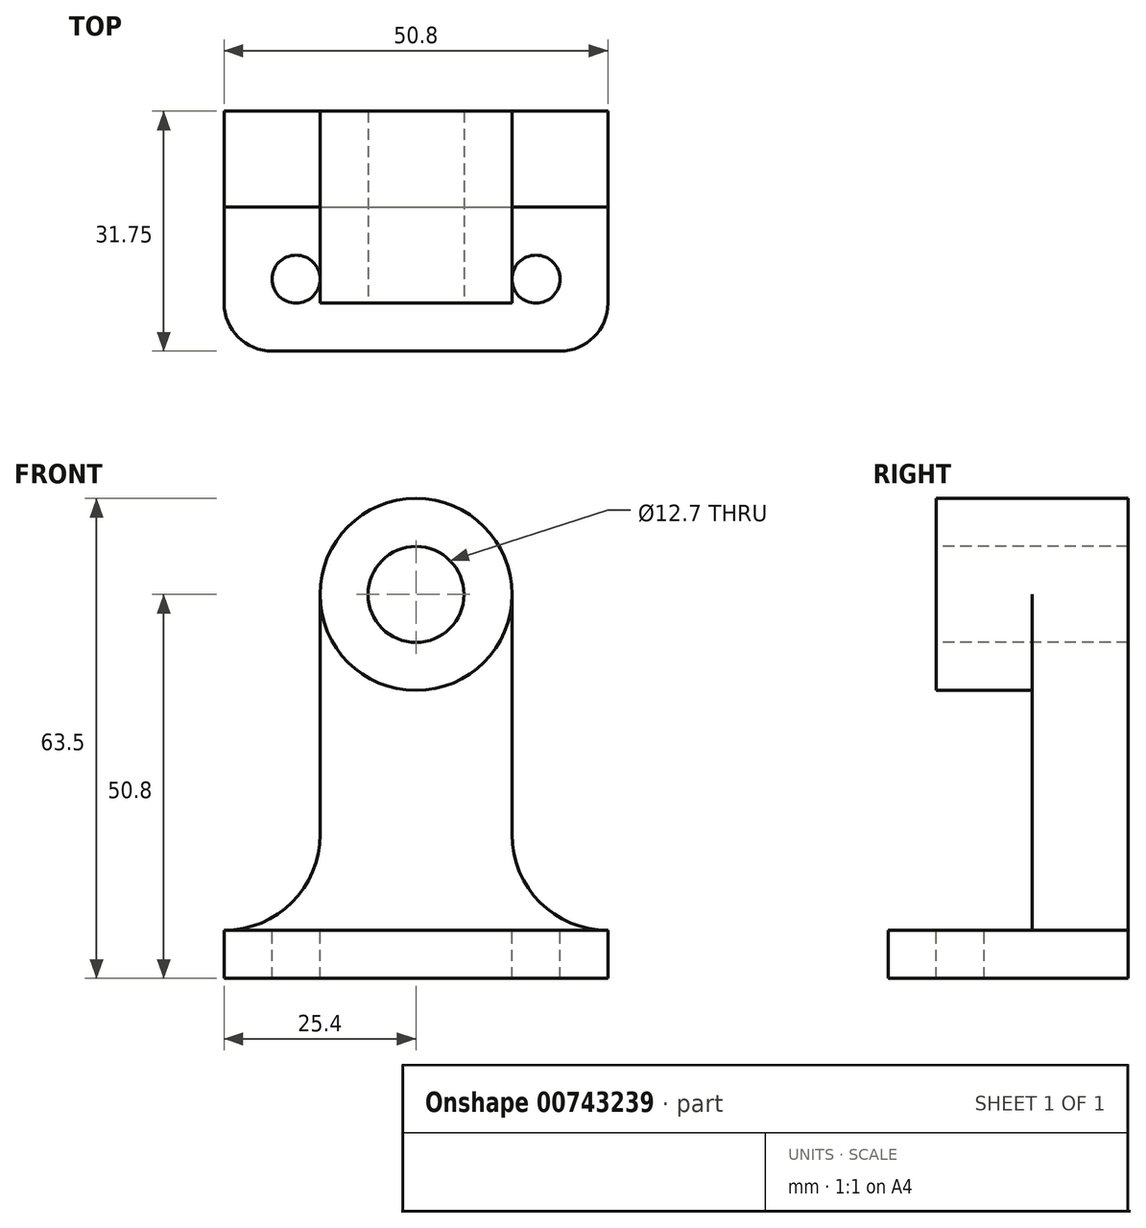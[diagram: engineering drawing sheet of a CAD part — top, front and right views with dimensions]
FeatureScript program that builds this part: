
annotation { "Feature Type Name" : "Feature", "Feature Type Description" : "" }
export const myFeature = defineFeature(function(context is Context, id is Id, definition is map)
    precondition{}
    {
        {
            var Q0;
            Q0=qCreatedBy(makeId("Top.planeOp"),FACE);
            var sketch = newSketch(context, id + "F0", { "sketchPlane" : qUnion([Q0])});
            skLineSegment(sketch, "E0.bottom", {"start": v(0, 0) * mm, "end": v(50.8, 0) * mm});
            skLineSegment(sketch, "E0.top", {"start": v(0, -25.4) * mm, "end": v(50.8, -25.4) * mm});
            skLineSegment(sketch, "E0.left", {"start": v(0, 0) * mm, "end": v(0, -25.4) * mm});
            skLineSegment(sketch, "E0.right", {"start": v(50.8, 0) * mm, "end": v(50.8, -25.4) * mm});
            skCircle(sketch, "E1", {"center": v(6.35, -25.4) * mm, "radius": 6.35 * mm});
            skCircle(sketch, "E2", {"center": v(44.45, -25.4) * mm, "radius": 6.35 * mm});
            skLineSegment(sketch, "E3.bottom", {"start": v(6.35, -25.4) * mm, "end": v(44.45, -25.4) * mm});
            skLineSegment(sketch, "E3.top", {"start": v(6.35, -31.75) * mm, "end": v(44.45, -31.75) * mm});
            skLineSegment(sketch, "E3.left", {"start": v(6.35, -25.4) * mm, "end": v(6.35, -31.75) * mm});
            skLineSegment(sketch, "E3.right", {"start": v(44.45, -25.4) * mm, "end": v(44.45, -31.75) * mm});
            skSolve(sketch);
        }
        {
            var Q0;
            Q0=makeQuery(id+"F0.imprint","IMPRINT",FACE,{"disambiguationData":[TD([[makeQuery(id+"F0.imprint","IMPRINT",EDGE,{"derivedFrom":sQuery(id+"F0.wireOp",EDGE,"E0.bottom")}),-1.0]])]});
            var Q1;
            {var subQ0=sQuery(id+"F0.wireOp",EDGE,"E1");var subQ3=sQuery(id+"F0.wireOp",EDGE,"E3.bottom");var subQ5=makeQuery(id+"F0.imprint","INTERSECT",VERTEX,{"derivedFrom":[subQ0,subQ3]});Q1=makeQuery(id+"F0.imprint","IMPRINT",FACE,{"disambiguationData":[TD([[makeQuery(id+"F0.imprint","IMPRINT",EDGE,{"disambiguationData":[TD([[subQ5,-1.0]])],"derivedFrom":subQ0}),1.0]])]});}
            var Q2;
            {var subQ3=sQuery(id+"F0.wireOp",EDGE,"E3.left");Q2=makeQuery(id+"F0.imprint","IMPRINT",FACE,{"disambiguationData":[TD([[makeQuery(id+"F0.imprint","IMPRINT",EDGE,{"derivedFrom":subQ3}),-1.0]])]});}
            var Q3;
            {var subQ0=sQuery(id+"F0.wireOp",EDGE,"E3.left");Q3=makeQuery(id+"F0.imprint","IMPRINT",FACE,{"disambiguationData":[TD([[makeQuery(id+"F0.imprint","IMPRINT",EDGE,{"derivedFrom":subQ0}),1.0]])]});}
            var Q4;
            {var subQ0=sQuery(id+"F0.wireOp",EDGE,"E3.top");Q4=makeQuery(id+"F0.imprint","IMPRINT",FACE,{"disambiguationData":[TD([[makeQuery(id+"F0.imprint","IMPRINT",EDGE,{"derivedFrom":subQ0}),1.0]])]});}
            var Q5;
            {var subQ0=sQuery(id+"F0.wireOp",EDGE,"E3.right");Q5=makeQuery(id+"F0.imprint","IMPRINT",FACE,{"disambiguationData":[TD([[makeQuery(id+"F0.imprint","IMPRINT",EDGE,{"derivedFrom":subQ0}),-1.0]])]});}
            var Q6;
            {var subQ3=sQuery(id+"F0.wireOp",EDGE,"E3.right");Q6=makeQuery(id+"F0.imprint","IMPRINT",FACE,{"disambiguationData":[TD([[makeQuery(id+"F0.imprint","IMPRINT",EDGE,{"derivedFrom":subQ3}),1.0]])]});}
            var Q7;
            {var subQ0=sQuery(id+"F0.wireOp",EDGE,"E2");var subQ3=sQuery(id+"F0.wireOp",EDGE,"E3.bottom");var subQ5=makeQuery(id+"F0.imprint","INTERSECT",VERTEX,{"derivedFrom":[subQ0,subQ3]});Q7=makeQuery(id+"F0.imprint","IMPRINT",FACE,{"disambiguationData":[TD([[makeQuery(id+"F0.imprint","IMPRINT",EDGE,{"disambiguationData":[TD([[subQ5,1.0]])],"derivedFrom":subQ0}),1.0]])]});}
            extrude(context, id + "F1", {"entities" : qUnion([Q0, Q1, Q2, Q3, Q4, Q5, Q6, Q7]), "depth" : 6.35 * mm, "offsetDistance" : 25.4 * mm});
        }
        {
            var Q0;
            Q0=qCreatedBy(makeId("Front.planeOp"),FACE);
            var sketch = newSketch(context, id + "F2", { "sketchPlane" : qUnion([Q0])});
            skLineSegment(sketch, "E4.bottom", {"start": v(12.7, 6.35) * mm, "end": v(38.1, 6.35) * mm});
            skLineSegment(sketch, "E4.top", {"start": v(12.7, 50.8) * mm, "end": v(38.1, 50.8) * mm});
            skLineSegment(sketch, "E4.left", {"start": v(12.7, 6.35) * mm, "end": v(12.7, 50.8) * mm});
            skLineSegment(sketch, "E4.right", {"start": v(38.1, 6.35) * mm, "end": v(38.1, 50.8) * mm});
            skCircle(sketch, "E5", {"center": v(25.4, 50.8) * mm, "radius": 12.7 * mm});
            skLineSegment(sketch, "E6.bottom", {"start": v(12.7, 50.8) * mm, "end": v(0, 50.8) * mm});
            skLineSegment(sketch, "E6.top", {"start": v(12.7, 6.35) * mm, "end": v(0, 6.35) * mm});
            skLineSegment(sketch, "E6.left", {"start": v(12.7, 50.8) * mm, "end": v(12.7, 6.35) * mm});
            skLineSegment(sketch, "E6.right", {"start": v(0, 50.8) * mm, "end": v(0, 6.35) * mm});
            skLineSegment(sketch, "E7.bottom", {"start": v(38.1, 50.8) * mm, "end": v(50.8, 50.8) * mm});
            skLineSegment(sketch, "E7.top", {"start": v(38.1, 6.35) * mm, "end": v(50.8, 6.35) * mm});
            skLineSegment(sketch, "E7.left", {"start": v(38.1, 50.8) * mm, "end": v(38.1, 6.35) * mm});
            skLineSegment(sketch, "E7.right", {"start": v(50.8, 50.8) * mm, "end": v(50.8, 6.35) * mm});
            skCircle(sketch, "E8", {"center": v(50.8, 19.05) * mm, "radius": 12.7 * mm});
            skCircle(sketch, "E9", {"center": v(0, 19.05) * mm, "radius": 12.7 * mm});
            skSolve(sketch);
        }
        {
            var Q0;
            {var subQ1=sQuery(id+"F2.wireOp",EDGE,"E4.bottom");Q0=makeQuery(id+"F2.imprint","IMPRINT",FACE,{"disambiguationData":[TD([[makeQuery(id+"F2.imprint","IMPRINT",EDGE,{"derivedFrom":subQ1}),1.0]])]});}
            var Q1;
            {var subQ0=sQuery(id+"F2.wireOp",EDGE,"E6.top");Q1=makeQuery(id+"F2.imprint","IMPRINT",FACE,{"disambiguationData":[TD([[makeQuery(id+"F2.imprint","IMPRINT",EDGE,{"derivedFrom":subQ0}),-1.0]])]});}
            var Q2;
            {var subQ0=sQuery(id+"F2.wireOp",EDGE,"E7.top");Q2=makeQuery(id+"F2.imprint","IMPRINT",FACE,{"disambiguationData":[TD([[makeQuery(id+"F2.imprint","IMPRINT",EDGE,{"derivedFrom":subQ0}),1.0]])]});}
            var Q3;
            {var subQ0=sQuery(id+"F2.wireOp",EDGE,"E4.top");Q3=makeQuery(id+"F2.imprint","IMPRINT",FACE,{"disambiguationData":[TD([[makeQuery(id+"F2.imprint","IMPRINT",EDGE,{"derivedFrom":subQ0}),1.0]])]});}
            var Q4;
            {var subQ0=sQuery(id+"F2.wireOp",EDGE,"E4.top");Q4=makeQuery(id+"F2.imprint","IMPRINT",FACE,{"disambiguationData":[TD([[makeQuery(id+"F2.imprint","IMPRINT",EDGE,{"derivedFrom":subQ0}),-1.0]])]});}
            extrude(context, id + "F3", {"entities" : qUnion([Q0, Q1, Q2, Q3, Q4]), "operationType" : NewBodyOperationType.ADD, "depth" : 12.7 * mm, "offsetDistance" : 25.4 * mm});
        }
        {
            var Q0;
            Q0=makeQuery(id+"F3.opExtrude","CAP_FACE",FACE,{"disambiguationData":[OSD([sQuery(id+"F2.wireOp",EDGE,"E4.bottom"),sQuery(id+"F2.wireOp",EDGE,"E5"),sQuery(id+"F2.wireOp",EDGE,"E6.top"),sQuery(id+"F2.wireOp",EDGE,"E6.left"),sQuery(id+"F2.wireOp",EDGE,"E7.top"),sQuery(id+"F2.wireOp",EDGE,"E7.left"),sQuery(id+"F2.wireOp",EDGE,"E8"),sQuery(id+"F2.wireOp",EDGE,"E9")])],"isStart":false});
            var sketch = newSketch(context, id + "F4", { "sketchPlane" : qUnion([Q0])});
            skCircle(sketch, "E10", {"center": v(25.4, 50.8) * mm, "radius": 12.7 * mm});
            skSolve(sketch);
        }
        {
            var Q0;
            {var subQ0=sQuery(id+"F4.wireOp",EDGE,"E10");var subQ1=makeQuery(id+"F4.imprint","INTERSECT",VERTEX,{"derivedFrom":[makeQuery(id+"F3.opExtrude","CAP_EDGE",EDGE,{"disambiguationData":[OSD([sQuery(id+"F2.wireOp",EDGE,"E6.left")])],"isStart":false}),subQ0]});Q0=makeQuery(id+"F4.imprint","IMPRINT",FACE,{"disambiguationData":[TD([[makeQuery(id+"F4.imprint","IMPRINT",EDGE,{"disambiguationData":[TD([[subQ1,1.0]])],"derivedFrom":subQ0}),1.0]])]});}
            extrude(context, id + "F5", {"entities" : qUnion([Q0]), "operationType" : NewBodyOperationType.ADD, "depth" : 12.7 * mm, "offsetDistance" : 25.4 * mm});
        }
        {
            var Q0;
            Q0=makeQuery(id+"F5.opExtrude","CAP_FACE",FACE,{"disambiguationData":[OSD([sQuery(id+"F4.wireOp",EDGE,"E10")])],"isStart":false});
            var sketch = newSketch(context, id + "F6", { "sketchPlane" : qUnion([Q0])});
            skCircle(sketch, "E11", {"center": v(25.4, 50.8) * mm, "radius": 6.35 * mm});
            skSolve(sketch);
        }
        {
            var Q0;
            Q0=makeQuery(id+"F6.imprint","IMPRINT",FACE,{"disambiguationData":[TD([[makeQuery(id+"F6.imprint","IMPRINT",EDGE,{"derivedFrom":sQuery(id+"F6.wireOp",EDGE,"E11")}),1.0]])]});
            extrude(context, id + "F7", {"entities" : qUnion([Q0]), "operationType" : NewBodyOperationType.REMOVE, "oppositeDirection" : true, "depth" : 25.4 * mm, "offsetDistance" : 25.4 * mm});
        }
        {
            var Q0;
            Q0=makeQuery(id+"F1.opExtrude","CAP_FACE",FACE,{"disambiguationData":[OSD([sQuery(id+"F0.wireOp",EDGE,"E0.bottom"),sQuery(id+"F0.wireOp",EDGE,"E0.left"),sQuery(id+"F0.wireOp",EDGE,"E0.right"),sQuery(id+"F0.wireOp",EDGE,"E1"),sQuery(id+"F0.wireOp",EDGE,"E2"),sQuery(id+"F0.wireOp",EDGE,"E3.top")])],"isStart":false});
            var sketch = newSketch(context, id + "F8", { "sketchPlane" : qUnion([Q0])});
            skCircle(sketch, "E12", {"center": v(41.28, -22.23) * mm, "radius": 3.17 * mm});
            skCircle(sketch, "E13", {"center": v(9.53, -22.23) * mm, "radius": 3.18 * mm});
            skSolve(sketch);
        }
        {
            var Q0;
            Q0=makeQuery(id+"F8.imprint","IMPRINT",FACE,{"disambiguationData":[TD([[makeQuery(id+"F8.imprint","IMPRINT",EDGE,{"derivedFrom":sQuery(id+"F8.wireOp",EDGE,"E13")}),1.0]])]});
            var Q1;
            Q1=makeQuery(id+"F8.imprint","IMPRINT",FACE,{"disambiguationData":[TD([[makeQuery(id+"F8.imprint","IMPRINT",EDGE,{"derivedFrom":sQuery(id+"F8.wireOp",EDGE,"E12")}),1.0]])]});
            extrude(context, id + "F9", {"entities" : qUnion([Q0, Q1]), "operationType" : NewBodyOperationType.REMOVE, "oppositeDirection" : true, "depth" : 6.35 * mm, "offsetDistance" : 25.4 * mm});
        }
    });
